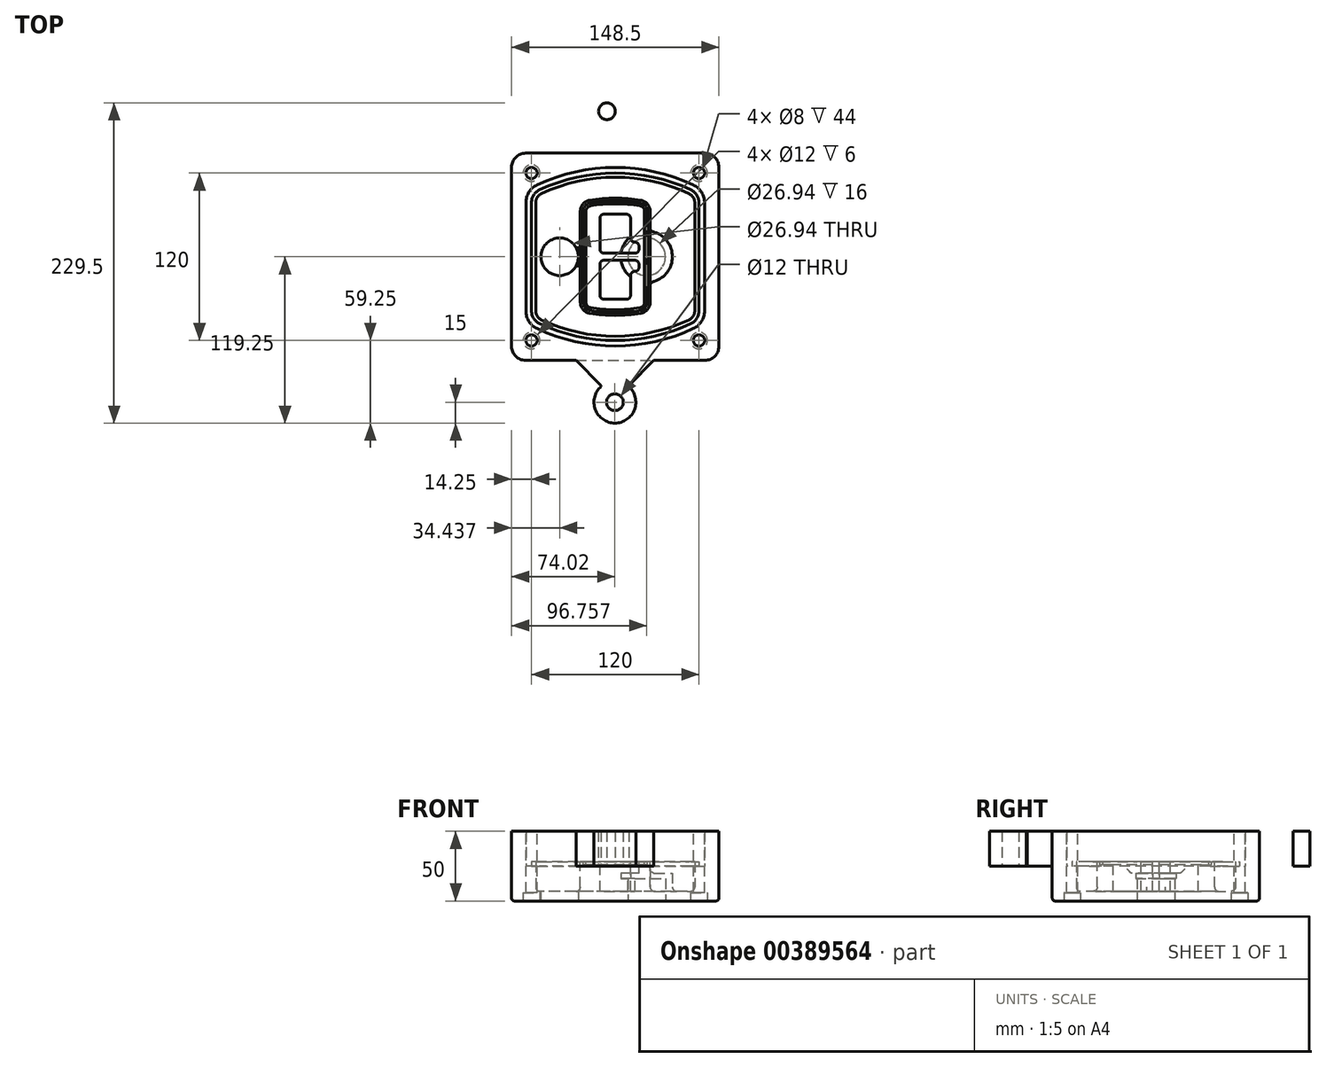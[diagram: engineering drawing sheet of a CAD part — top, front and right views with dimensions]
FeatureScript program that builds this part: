
annotation { "Feature Type Name" : "Feature", "Feature Type Description" : "" }
export const myFeature = defineFeature(function(context is Context, id is Id, definition is map)
    precondition{}
    {
        {
            var Q0;
            Q0=qCreatedBy(makeId("Top.planeOp"),FACE);
            var sketch = newSketch(context, id + "F0", { "sketchPlane" : qUnion([Q0])});
            skPoint(sketch, "E0.rect.middle", {"position": v(0, 0) * mm});
            skLineSegment(sketch, "E1.bottom", {"start": v(-64.25, -74.25) * mm, "end": v(64.25, -74.25) * mm});
            skLineSegment(sketch, "E1.top", {"start": v(-64.25, 74.25) * mm, "end": v(64.25, 74.25) * mm});
            skLineSegment(sketch, "E1.left", {"start": v(-74.25, -64.25) * mm, "end": v(-74.25, 64.25) * mm});
            skLineSegment(sketch, "E1.right", {"start": v(74.25, -64.25) * mm, "end": v(74.25, 64.25) * mm});
            skLineSegment(sketch, "E2", {"start": v(-74.25, 74.25) * mm, "end": v(74.25, -74.25) * mm, "construction": true});
            skLineSegment(sketch, "E3", {"start": v(74.25, 74.25) * mm, "end": v(-74.25, -74.25) * mm, "construction": true});
            skCircle(sketch, "E4", {"center": v(-60, 60) * mm, "radius": 4 * mm});
            skCircle(sketch, "E5", {"center": v(60, 60) * mm, "radius": 4 * mm});
            skCircle(sketch, "E6", {"center": v(60, -60) * mm, "radius": 4 * mm});
            skCircle(sketch, "E7", {"center": v(-60, -60) * mm, "radius": 4 * mm});
            skLineSegment(sketch, "E8", {"start": v(-60, 60) * mm, "end": v(60, 60) * mm, "construction": true});
            skLineSegment(sketch, "E9", {"start": v(60, 60) * mm, "end": v(60, -60) * mm, "construction": true});
            skLineSegment(sketch, "E10", {"start": v(60, -60) * mm, "end": v(-60, -60) * mm, "construction": true});
            skLineSegment(sketch, "E11", {"start": v(-60, -60) * mm, "end": v(-60, 60) * mm, "construction": true});
            skLineSegment(sketch, "E12", {"start": v(-60, 38.83) * mm, "end": v(-60, -38.83) * mm});
            skLineSegment(sketch, "E13", {"start": v(60, 38.83) * mm, "end": v(60, -38.83) * mm});
            skArc(sketch, "E14", {"start": v(54.26, 47.88) * mm, "mid": v(0, 60) * mm, "end": v(-54.26, 47.88) * mm});
            skArc(sketch, "E15", {"start": v(-54.26, -47.88) * mm, "mid": v(0, -60) * mm, "end": v(54.26, -47.88) * mm});
            skLineSegment(sketch, "E16", {"start": v(-60, 0) * mm, "end": v(60, 0) * mm, "construction": true});
            skPoint(sketch, "E17.visualSharp", {"position": v(-60, -45) * mm});
            skArc(sketch, "E17.filletArc", {"start": v(-60, -38.83) * mm, "mid": v(-58.44, -44.2) * mm, "end": v(-54.26, -47.88) * mm});
            skPoint(sketch, "E18.visualSharp", {"position": v(-60, 45) * mm});
            skArc(sketch, "E18.filletArc", {"start": v(-54.26, 47.88) * mm, "mid": v(-58.44, 44.2) * mm, "end": v(-60, 38.83) * mm});
            skPoint(sketch, "E19.visualSharp", {"position": v(60, 45) * mm});
            skArc(sketch, "E19.filletArc", {"start": v(60, 38.83) * mm, "mid": v(58.44, 44.2) * mm, "end": v(54.26, 47.88) * mm});
            skPoint(sketch, "E20.visualSharp", {"position": v(60, -45) * mm});
            skArc(sketch, "E20.filletArc", {"start": v(54.26, -47.88) * mm, "mid": v(58.44, -44.2) * mm, "end": v(60, -38.83) * mm});
            skPoint(sketch, "E21.visualSharp", {"position": v(-74.25, 74.25) * mm});
            skArc(sketch, "E21.filletArc", {"start": v(-64.25, 74.25) * mm, "mid": v(-71.32, 71.32) * mm, "end": v(-74.25, 64.25) * mm});
            skPoint(sketch, "E22.visualSharp", {"position": v(74.25, 74.25) * mm});
            skArc(sketch, "E22.filletArc", {"start": v(74.25, 64.25) * mm, "mid": v(71.32, 71.32) * mm, "end": v(64.25, 74.25) * mm});
            skPoint(sketch, "E23.visualSharp", {"position": v(74.25, -74.25) * mm});
            skArc(sketch, "E23.filletArc", {"start": v(64.25, -74.25) * mm, "mid": v(71.32, -71.32) * mm, "end": v(74.25, -64.25) * mm});
            skPoint(sketch, "E24.visualSharp", {"position": v(-74.25, -74.25) * mm});
            skArc(sketch, "E24.filletArc", {"start": v(-74.25, -64.25) * mm, "mid": v(-71.32, -71.32) * mm, "end": v(-64.25, -74.25) * mm});
            skArc(sketch, "E25.0", {"start": v(57, 38.83) * mm, "mid": v(55.9, 42.58) * mm, "end": v(52.98, 45.17) * mm});
            skLineSegment(sketch, "E25.1", {"start": v(57, 38.83) * mm, "end": v(57, -38.83) * mm});
            skArc(sketch, "E25.2", {"start": v(52.98, -45.17) * mm, "mid": v(55.9, -42.58) * mm, "end": v(57, -38.83) * mm});
            skArc(sketch, "E25.3", {"start": v(-52.98, -45.17) * mm, "mid": v(0, -57) * mm, "end": v(52.98, -45.17) * mm});
            skArc(sketch, "E25.4", {"start": v(-57, -38.83) * mm, "mid": v(-55.9, -42.58) * mm, "end": v(-52.98, -45.17) * mm});
            skArc(sketch, "E25.5", {"start": v(52.98, 45.17) * mm, "mid": v(0, 57) * mm, "end": v(-52.98, 45.17) * mm});
            skLineSegment(sketch, "E25.6", {"start": v(-57, 38.83) * mm, "end": v(-57, -38.83) * mm});
            skArc(sketch, "E25.7", {"start": v(-52.98, 45.17) * mm, "mid": v(-55.9, 42.58) * mm, "end": v(-57, 38.83) * mm});
            skArc(sketch, "E26.0", {"start": v(-55.96, 51.5) * mm, "mid": v(-61.82, 46.33) * mm, "end": v(-64, 38.83) * mm});
            skArc(sketch, "E26.1", {"start": v(55.96, 51.5) * mm, "mid": v(0, 64) * mm, "end": v(-55.96, 51.5) * mm});
            skArc(sketch, "E26.2", {"start": v(64, 38.83) * mm, "mid": v(61.82, 46.33) * mm, "end": v(55.96, 51.5) * mm});
            skLineSegment(sketch, "E26.3", {"start": v(64, 38.83) * mm, "end": v(64, -38.83) * mm});
            skArc(sketch, "E26.4", {"start": v(55.96, -51.5) * mm, "mid": v(61.82, -46.33) * mm, "end": v(64, -38.83) * mm});
            skLineSegment(sketch, "E26.5", {"start": v(-64, 38.83) * mm, "end": v(-64, -38.83) * mm});
            skArc(sketch, "E26.6", {"start": v(-55.96, -51.5) * mm, "mid": v(0, -64) * mm, "end": v(55.96, -51.5) * mm});
            skArc(sketch, "E26.7", {"start": v(-64, -38.83) * mm, "mid": v(-61.82, -46.33) * mm, "end": v(-55.96, -51.5) * mm});
            skLineSegment(sketch, "E27", {"start": v(9.02, 104.25) * mm, "end": v(9.02, 90.33) * mm, "construction": true});
            skLineSegment(sketch, "E28", {"start": v(9.02, 90.33) * mm, "end": v(25.1, 74.25) * mm});
            skLineSegment(sketch, "E29", {"start": v(-20.98, 104.25) * mm, "end": v(-20.98, 92.25) * mm});
            skLineSegment(sketch, "E30", {"start": v(-20.98, 92.25) * mm, "end": v(-38.98, 74.25) * mm});
            skArc(sketch, "E31", {"start": v(9.02, 104.25) * mm, "mid": v(-5.98, 119.25) * mm, "end": v(-20.98, 104.25) * mm});
            skCircle(sketch, "E32", {"center": v(-5.98, 104.25) * mm, "radius": 6 * mm});
            skPoint(sketch, "E33.positionSnap0", {"position": v(0, -74.25) * mm});
            skLineSegment(sketch, "E34", {"start": v(9.64, -92.95) * mm, "end": v(9.64, -92.25) * mm});
            skLineSegment(sketch, "E35", {"start": v(9.64, -92.25) * mm, "end": v(27.64, -74.25) * mm});
            skLineSegment(sketch, "E36", {"start": v(-10.1, -92.95) * mm, "end": v(-10.1, -92.25) * mm});
            skLineSegment(sketch, "E37", {"start": v(-10.1, -92.25) * mm, "end": v(-28.1, -74.25) * mm});
            skArc(sketch, "E38", {"start": v(-10.1, -92.95) * mm, "mid": v(-0.23, -119.25) * mm, "end": v(9.64, -92.95) * mm});
            skCircle(sketch, "E39", {"center": v(-0.23, -104.25) * mm, "radius": 6 * mm});
            skSolve(sketch);
        }
        {
            var Q0;
            Q0=makeQuery(id+"F0.imprint","IMPRINT",FACE,{"disambiguationData":[TD([[makeQuery(id+"F0.imprint","IMPRINT",EDGE,{"derivedFrom":sQuery(id+"F0.wireOp",EDGE,"E1.bottom")}),1.0]])]});
            var Q1;
            Q1=makeQuery(id+"F0.imprint","IMPRINT",FACE,{"disambiguationData":[TD([[makeQuery(id+"F0.imprint","IMPRINT",EDGE,{"derivedFrom":sQuery(id+"F0.wireOp",EDGE,"E12")}),1.0]])]});
            var Q2;
            Q2=makeQuery(id+"F0.imprint","IMPRINT",FACE,{"disambiguationData":[TD([[makeQuery(id+"F0.imprint","IMPRINT",EDGE,{"derivedFrom":sQuery(id+"F0.wireOp",EDGE,"E25.0")}),1.0]])]});
            var Q3;
            Q3=makeQuery(id+"F0.imprint","IMPRINT",FACE,{"disambiguationData":[TD([[makeQuery(id+"F0.imprint","IMPRINT",EDGE,{"derivedFrom":sQuery(id+"F0.wireOp",EDGE,"E12")}),-1.0]])]});
            extrude(context, id + "F1", {"entities" : qUnion([Q0, Q1, Q2, Q3]), "oppositeDirection" : true, "depth" : 25 * mm});
        }
        {
            var Q0;
            Q0=makeQuery(id+"F0.imprint","IMPRINT",FACE,{"disambiguationData":[TD([[makeQuery(id+"F0.imprint","IMPRINT",EDGE,{"derivedFrom":sQuery(id+"F0.wireOp",EDGE,"E12")}),1.0]])]});
            extrude(context, id + "F2", {"entities" : qUnion([Q0]), "operationType" : NewBodyOperationType.ADD, "depth" : 3 * mm});
        }
        {
            var Q0;
            Q0=makeQuery(id+"F0.imprint","IMPRINT",FACE,{"disambiguationData":[TD([[makeQuery(id+"F0.imprint","IMPRINT",EDGE,{"derivedFrom":sQuery(id+"F0.wireOp",EDGE,"E25.0")}),1.0]])]});
            extrude(context, id + "F3", {"entities" : qUnion([Q0]), "operationType" : NewBodyOperationType.REMOVE, "oppositeDirection" : true, "depth" : 18 * mm});
        }
        {
            var Q0;
            Q0=makeQuery(id+"F2.opExtrude","CAP_FACE",FACE,{"disambiguationData":[OSD([sQuery(id+"F0.wireOp",EDGE,"E12"),sQuery(id+"F0.wireOp",EDGE,"E13"),sQuery(id+"F0.wireOp",EDGE,"E14"),sQuery(id+"F0.wireOp",EDGE,"E15"),sQuery(id+"F0.wireOp",EDGE,"E17.filletArc"),sQuery(id+"F0.wireOp",EDGE,"E18.filletArc"),sQuery(id+"F0.wireOp",EDGE,"E19.filletArc"),sQuery(id+"F0.wireOp",EDGE,"E20.filletArc"),sQuery(id+"F0.wireOp",EDGE,"E25.0"),sQuery(id+"F0.wireOp",EDGE,"E25.1"),sQuery(id+"F0.wireOp",EDGE,"E25.2"),sQuery(id+"F0.wireOp",EDGE,"E25.3"),sQuery(id+"F0.wireOp",EDGE,"E25.4"),sQuery(id+"F0.wireOp",EDGE,"E25.5"),sQuery(id+"F0.wireOp",EDGE,"E25.6"),sQuery(id+"F0.wireOp",EDGE,"E25.7")])],"isStart":false});
            var sketch = newSketch(context, id + "F4", { "sketchPlane" : qUnion([Q0])});
            skArc(sketch, "E40.0", {"start": v(-18.34, -40.45) * mm, "mid": v(0, -42) * mm, "end": v(18.34, -40.45) * mm});
            skArc(sketch, "E41.0", {"start": v(18.34, 40.45) * mm, "mid": v(0, 42) * mm, "end": v(-18.34, 40.45) * mm});
            skLineSegment(sketch, "E42", {"start": v(-25, 32.57) * mm, "end": v(-25, -32.57) * mm});
            skLineSegment(sketch, "E43", {"start": v(25, 32.57) * mm, "end": v(25, -32.57) * mm});
            skLineSegment(sketch, "E44", {"start": v(-25, 39.1) * mm, "end": v(25, 39.1) * mm, "construction": true});
            skLineSegment(sketch, "E45", {"start": v(-25, -39.1) * mm, "end": v(25, -39.1) * mm, "construction": true});
            skPoint(sketch, "E46.visualSharp", {"position": v(-25, 39.1) * mm});
            skArc(sketch, "E46.filletArc", {"start": v(-18.34, 40.45) * mm, "mid": v(-23.11, 37.73) * mm, "end": v(-25, 32.57) * mm});
            skPoint(sketch, "E47.visualSharp", {"position": v(25, 39.1) * mm});
            skArc(sketch, "E47.filletArc", {"start": v(25, 32.57) * mm, "mid": v(23.11, 37.73) * mm, "end": v(18.34, 40.45) * mm});
            skPoint(sketch, "E48.visualSharp", {"position": v(25, -39.1) * mm});
            skArc(sketch, "E48.filletArc", {"start": v(18.34, -40.45) * mm, "mid": v(23.11, -37.73) * mm, "end": v(25, -32.57) * mm});
            skPoint(sketch, "E49.visualSharp", {"position": v(-25, -39.1) * mm});
            skArc(sketch, "E49.filletArc", {"start": v(-25, -32.57) * mm, "mid": v(-23.11, -37.73) * mm, "end": v(-18.34, -40.45) * mm});
            skArc(sketch, "E50.0", {"start": v(52.98, 45.17) * mm, "mid": v(0, 57) * mm, "end": v(-52.98, 45.17) * mm});
            skArc(sketch, "E50.1", {"start": v(-52.98, 45.17) * mm, "mid": v(-55.9, 42.58) * mm, "end": v(-57, 38.83) * mm});
            skLineSegment(sketch, "E50.2", {"start": v(-57, 38.83) * mm, "end": v(-57, -38.83) * mm});
            skArc(sketch, "E50.3", {"start": v(-57, -38.83) * mm, "mid": v(-55.9, -42.58) * mm, "end": v(-52.98, -45.17) * mm});
            skArc(sketch, "E50.4", {"start": v(-52.98, -45.17) * mm, "mid": v(0, -57) * mm, "end": v(52.98, -45.17) * mm});
            skArc(sketch, "E50.5", {"start": v(52.98, -45.17) * mm, "mid": v(55.9, -42.58) * mm, "end": v(57, -38.83) * mm});
            skLineSegment(sketch, "E50.6", {"start": v(57, 38.83) * mm, "end": v(57, -38.83) * mm});
            skArc(sketch, "E50.7", {"start": v(57, 38.83) * mm, "mid": v(55.9, 42.58) * mm, "end": v(52.98, 45.17) * mm});
            skLineSegment(sketch, "E51.0", {"start": v(23, 32.57) * mm, "end": v(23, -32.57) * mm});
            skArc(sketch, "E51.1", {"start": v(18, -38.48) * mm, "mid": v(21.58, -36.44) * mm, "end": v(23, -32.57) * mm});
            skArc(sketch, "E51.2", {"start": v(-18, -38.48) * mm, "mid": v(0, -40) * mm, "end": v(18, -38.48) * mm});
            skArc(sketch, "E51.3", {"start": v(-23, -32.57) * mm, "mid": v(-21.58, -36.44) * mm, "end": v(-18, -38.48) * mm});
            skLineSegment(sketch, "E51.4", {"start": v(-23, 32.57) * mm, "end": v(-23, -32.57) * mm});
            skArc(sketch, "E51.5", {"start": v(23, 32.57) * mm, "mid": v(21.58, 36.44) * mm, "end": v(18, 38.48) * mm});
            skArc(sketch, "E51.6", {"start": v(-18, 38.48) * mm, "mid": v(-21.58, 36.44) * mm, "end": v(-23, 32.57) * mm});
            skArc(sketch, "E51.7", {"start": v(18, 38.48) * mm, "mid": v(0, 40) * mm, "end": v(-18, 38.48) * mm});
            skArc(sketch, "E52.0", {"start": v(21, 32.57) * mm, "mid": v(20.06, 35.15) * mm, "end": v(17.67, 36.5) * mm});
            skLineSegment(sketch, "E52.1", {"start": v(21, 32.57) * mm, "end": v(21, -32.57) * mm});
            skArc(sketch, "E52.2", {"start": v(17.67, -36.5) * mm, "mid": v(20.06, -35.15) * mm, "end": v(21, -32.57) * mm});
            skArc(sketch, "E52.3", {"start": v(-17.67, -36.5) * mm, "mid": v(0, -38) * mm, "end": v(17.67, -36.5) * mm});
            skArc(sketch, "E52.4", {"start": v(-21, -32.57) * mm, "mid": v(-20.06, -35.15) * mm, "end": v(-17.67, -36.5) * mm});
            skArc(sketch, "E52.5", {"start": v(17.67, 36.5) * mm, "mid": v(0, 38) * mm, "end": v(-17.67, 36.5) * mm});
            skLineSegment(sketch, "E52.6", {"start": v(-21, 32.57) * mm, "end": v(-21, -32.57) * mm});
            skArc(sketch, "E52.7", {"start": v(-17.67, 36.5) * mm, "mid": v(-20.06, 35.15) * mm, "end": v(-21, 32.57) * mm});
            skLineSegment(sketch, "E53", {"start": v(-25, 0) * mm, "end": v(25, 0) * mm, "construction": true});
            skLineSegment(sketch, "E54", {"start": v(-11, 5.5) * mm, "end": v(-11, 27.5) * mm});
            skLineSegment(sketch, "E55", {"start": v(-8, 30.5) * mm, "end": v(8, 30.5) * mm});
            skLineSegment(sketch, "E56", {"start": v(11, 27.5) * mm, "end": v(11, 13.5) * mm});
            skLineSegment(sketch, "E57", {"start": v(14, 10.5) * mm, "end": v(14, 10.5) * mm});
            skLineSegment(sketch, "E58", {"start": v(17, 7.5) * mm, "end": v(17, 5.5) * mm});
            skLineSegment(sketch, "E59", {"start": v(14, 2.5) * mm, "end": v(-8, 2.5) * mm});
            skPoint(sketch, "E60.visualSharp", {"position": v(-11, 30.5) * mm});
            skArc(sketch, "E60.filletArc", {"start": v(-8, 30.5) * mm, "mid": v(-10.12, 29.62) * mm, "end": v(-11, 27.5) * mm});
            skPoint(sketch, "E61.visualSharp", {"position": v(11, 30.5) * mm});
            skArc(sketch, "E61.filletArc", {"start": v(11, 27.5) * mm, "mid": v(10.12, 29.62) * mm, "end": v(8, 30.5) * mm});
            skPoint(sketch, "E62.visualSharp", {"position": v(11, 10.5) * mm});
            skArc(sketch, "E62.filletArc", {"start": v(11, 13.5) * mm, "mid": v(11.88, 11.38) * mm, "end": v(14, 10.5) * mm});
            skPoint(sketch, "E63.visualSharp", {"position": v(17, 10.5) * mm});
            skArc(sketch, "E63.filletArc", {"start": v(17, 7.5) * mm, "mid": v(16.12, 9.62) * mm, "end": v(14, 10.5) * mm});
            skPoint(sketch, "E64.visualSharp", {"position": v(17, 2.5) * mm});
            skArc(sketch, "E64.filletArc", {"start": v(14, 2.5) * mm, "mid": v(16.12, 3.38) * mm, "end": v(17, 5.5) * mm});
            skPoint(sketch, "E65.visualSharp", {"position": v(-11, 2.5) * mm});
            skArc(sketch, "E65.filletArc", {"start": v(-11, 5.5) * mm, "mid": v(-10.12, 3.38) * mm, "end": v(-8, 2.5) * mm});
            skLineSegment(sketch, "E66.0.MirrorCS", {"start": v(14, -2.5) * mm, "end": v(-8, -2.5) * mm});
            skArc(sketch, "E67.0.MirrorCS", {"start": v(-11, -5.5) * mm, "mid": v(-10.12, -3.38) * mm, "end": v(-8, -2.5) * mm});
            skLineSegment(sketch, "E68.0.MirrorCS", {"start": v(-11, -5.5) * mm, "end": v(-11, -27.5) * mm});
            skArc(sketch, "E69.0.MirrorCS", {"start": v(-8, -30.5) * mm, "mid": v(-10.12, -29.62) * mm, "end": v(-11, -27.5) * mm});
            skLineSegment(sketch, "E70.0.MirrorCS", {"start": v(-8, -30.5) * mm, "end": v(8, -30.5) * mm});
            skArc(sketch, "E71.0.MirrorCS", {"start": v(11, -27.5) * mm, "mid": v(10.12, -29.62) * mm, "end": v(8, -30.5) * mm});
            skLineSegment(sketch, "E72.0.MirrorCS", {"start": v(11, -27.5) * mm, "end": v(11, -13.5) * mm});
            skArc(sketch, "E73.0.MirrorCS", {"start": v(11, -13.5) * mm, "mid": v(11.88, -11.38) * mm, "end": v(14, -10.5) * mm});
            skArc(sketch, "E74.0.MirrorCS", {"start": v(17, -7.5) * mm, "mid": v(16.12, -9.62) * mm, "end": v(14, -10.5) * mm});
            skLineSegment(sketch, "E75.0.MirrorCS", {"start": v(17, -7.5) * mm, "end": v(17, -5.5) * mm});
            skArc(sketch, "E76.0.MirrorCS", {"start": v(14, -2.5) * mm, "mid": v(16.12, -3.38) * mm, "end": v(17, -5.5) * mm});
            skSolve(sketch);
        }
        {
            var Q0;
            Q0=makeQuery(id+"F4.imprint","IMPRINT",FACE,{"disambiguationData":[TD([[makeQuery(id+"F4.imprint","IMPRINT",EDGE,{"derivedFrom":sQuery(id+"F4.wireOp",EDGE,"E40.0")}),1.0]])]});
            var Q1;
            Q1=makeQuery(id+"F4.imprint","IMPRINT",FACE,{"disambiguationData":[TD([[makeQuery(id+"F4.imprint","IMPRINT",EDGE,{"derivedFrom":sQuery(id+"F4.wireOp",EDGE,"E51.0")}),-1.0]])]});
            var Q2;
            Q2=makeQuery(id+"F4.imprint","IMPRINT",FACE,{"disambiguationData":[TD([[makeQuery(id+"F4.imprint","IMPRINT",EDGE,{"derivedFrom":sQuery(id+"F4.wireOp",EDGE,"E52.0")}),1.0]])]});
            extrude(context, id + "F5", {"entities" : qUnion([Q0, Q1, Q2]), "operationType" : NewBodyOperationType.ADD, "endBound" : BoundingType.UP_TO_NEXT, "oppositeDirection" : true, "depth" : 25 * mm});
        }
        {
            var Q0;
            Q0=makeQuery(id+"F4.imprint","IMPRINT",FACE,{"disambiguationData":[TD([[makeQuery(id+"F4.imprint","IMPRINT",EDGE,{"derivedFrom":sQuery(id+"F4.wireOp",EDGE,"E51.0")}),-1.0]])]});
            extrude(context, id + "F6", {"entities" : qUnion([Q0]), "operationType" : NewBodyOperationType.REMOVE, "oppositeDirection" : true, "depth" : 2 * mm});
        }
        {
            var Q0;
            Q0=makeQuery(id+"F1.opExtrude","CAP_FACE",FACE,{"disambiguationData":[OSD([sQuery(id+"F0.wireOp",EDGE,"E1.bottom"),sQuery(id+"F0.wireOp",EDGE,"E1.top"),sQuery(id+"F0.wireOp",EDGE,"E1.left"),sQuery(id+"F0.wireOp",EDGE,"E1.right"),sQuery(id+"F0.wireOp",EDGE,"E4"),sQuery(id+"F0.wireOp",EDGE,"E5"),sQuery(id+"F0.wireOp",EDGE,"E6"),sQuery(id+"F0.wireOp",EDGE,"E7"),sQuery(id+"F0.wireOp",EDGE,"E21.filletArc"),sQuery(id+"F0.wireOp",EDGE,"E22.filletArc"),sQuery(id+"F0.wireOp",EDGE,"E23.filletArc"),sQuery(id+"F0.wireOp",EDGE,"E24.filletArc")])],"isStart":false});
            var sketch = newSketch(context, id + "F7", { "sketchPlane" : qUnion([Q0])});
            skCircle(sketch, "E77", {"center": v(22.5, 0) * mm, "radius": 13.47 * mm});
            skCircle(sketch, "E78", {"center": v(-39.81, 0) * mm, "radius": 13.47 * mm});
            skLineSegment(sketch, "E79", {"start": v(74.25, 0) * mm, "end": v(-74.25, 0) * mm});
            skCircle(sketch, "E80", {"center": v(22.5, 0) * mm, "radius": 18.47 * mm});
            skCircle(sketch, "E81", {"center": v(60, -60) * mm, "radius": 6 * mm});
            skCircle(sketch, "E82", {"center": v(-60, -60) * mm, "radius": 6 * mm});
            skCircle(sketch, "E83", {"center": v(-60, 60) * mm, "radius": 6 * mm});
            skCircle(sketch, "E84", {"center": v(60, 60) * mm, "radius": 6 * mm});
            skSolve(sketch);
        }
        {
            var Q0;
            {var subQ1=sQuery(id+"F7.wireOp",EDGE,"E79");var subQ4=sQuery(id+"F7.wireOp",EDGE,"E77");var subQ6=makeQuery(id+"F7.imprint","INTERSECT",VERTEX,{"disambiguationData":[OD(0.0)],"derivedFrom":[subQ4,subQ1]});Q0=makeQuery(id+"F7.imprint","IMPRINT",FACE,{"disambiguationData":[TD([[makeQuery(id+"F7.imprint","IMPRINT",EDGE,{"disambiguationData":[TD([[subQ6,-1.0]])],"derivedFrom":subQ4}),-1.0]])]});}
            var Q1;
            {var subQ0=sQuery(id+"F7.wireOp",EDGE,"E79");var subQ1=sQuery(id+"F7.wireOp",EDGE,"E77");var subQ3=makeQuery(id+"F7.imprint","INTERSECT",VERTEX,{"disambiguationData":[OD(0.0)],"derivedFrom":[subQ1,subQ0]});Q1=makeQuery(id+"F7.imprint","IMPRINT",FACE,{"disambiguationData":[TD([[makeQuery(id+"F7.imprint","IMPRINT",EDGE,{"disambiguationData":[TD([[subQ3,-1.0]])],"derivedFrom":subQ1}),1.0]])]});}
            var Q2;
            {var subQ0=sQuery(id+"F7.wireOp",EDGE,"E79");var subQ1=sQuery(id+"F7.wireOp",EDGE,"E77");var subQ3=makeQuery(id+"F7.imprint","INTERSECT",VERTEX,{"disambiguationData":[OD(0.0)],"derivedFrom":[subQ1,subQ0]});Q2=makeQuery(id+"F7.imprint","IMPRINT",FACE,{"disambiguationData":[TD([[makeQuery(id+"F7.imprint","IMPRINT",EDGE,{"disambiguationData":[TD([[subQ3,1.0]])],"derivedFrom":subQ1}),1.0]])]});}
            var Q3;
            {var subQ1=sQuery(id+"F7.wireOp",EDGE,"E79");var subQ4=sQuery(id+"F7.wireOp",EDGE,"E77");var subQ6=makeQuery(id+"F7.imprint","INTERSECT",VERTEX,{"disambiguationData":[OD(0.0)],"derivedFrom":[subQ4,subQ1]});Q3=makeQuery(id+"F7.imprint","IMPRINT",FACE,{"disambiguationData":[TD([[makeQuery(id+"F7.imprint","IMPRINT",EDGE,{"disambiguationData":[TD([[subQ6,1.0]])],"derivedFrom":subQ4}),-1.0]])]});}
            extrude(context, id + "F8", {"entities" : qUnion([Q0, Q1, Q2, Q3]), "operationType" : NewBodyOperationType.ADD, "oppositeDirection" : true, "depth" : 20 * mm});
        }
        {
            var Q0;
            {var subQ0=sQuery(id+"F7.wireOp",EDGE,"E79");var subQ1=sQuery(id+"F7.wireOp",EDGE,"E77");var subQ3=makeQuery(id+"F7.imprint","INTERSECT",VERTEX,{"disambiguationData":[OD(0.0)],"derivedFrom":[subQ1,subQ0]});Q0=makeQuery(id+"F7.imprint","IMPRINT",FACE,{"disambiguationData":[TD([[makeQuery(id+"F7.imprint","IMPRINT",EDGE,{"disambiguationData":[TD([[subQ3,-1.0]])],"derivedFrom":subQ1}),1.0]])]});}
            var Q1;
            {var subQ0=sQuery(id+"F7.wireOp",EDGE,"E79");var subQ1=sQuery(id+"F7.wireOp",EDGE,"E77");var subQ3=makeQuery(id+"F7.imprint","INTERSECT",VERTEX,{"disambiguationData":[OD(0.0)],"derivedFrom":[subQ1,subQ0]});Q1=makeQuery(id+"F7.imprint","IMPRINT",FACE,{"disambiguationData":[TD([[makeQuery(id+"F7.imprint","IMPRINT",EDGE,{"disambiguationData":[TD([[subQ3,1.0]])],"derivedFrom":subQ1}),1.0]])]});}
            extrude(context, id + "F9", {"entities" : qUnion([Q0, Q1]), "operationType" : NewBodyOperationType.REMOVE, "oppositeDirection" : true, "depth" : 16 * mm});
        }
        {
            var Q0;
            {var subQ0=sQuery(id+"F7.wireOp",EDGE,"E79");var subQ1=sQuery(id+"F7.wireOp",EDGE,"E78");var subQ3=makeQuery(id+"F7.imprint","INTERSECT",VERTEX,{"disambiguationData":[OD(0.0)],"derivedFrom":[subQ1,subQ0]});Q0=makeQuery(id+"F7.imprint","IMPRINT",FACE,{"disambiguationData":[TD([[makeQuery(id+"F7.imprint","IMPRINT",EDGE,{"disambiguationData":[TD([[subQ3,-1.0]])],"derivedFrom":subQ1}),1.0]])]});}
            var Q1;
            {var subQ0=sQuery(id+"F7.wireOp",EDGE,"E79");var subQ1=sQuery(id+"F7.wireOp",EDGE,"E78");var subQ3=makeQuery(id+"F7.imprint","INTERSECT",VERTEX,{"disambiguationData":[OD(0.0)],"derivedFrom":[subQ1,subQ0]});Q1=makeQuery(id+"F7.imprint","IMPRINT",FACE,{"disambiguationData":[TD([[makeQuery(id+"F7.imprint","IMPRINT",EDGE,{"disambiguationData":[TD([[subQ3,1.0]])],"derivedFrom":subQ1}),1.0]])]});}
            extrude(context, id + "F10", {"entities" : qUnion([Q0, Q1]), "operationType" : NewBodyOperationType.REMOVE, "oppositeDirection" : true, "depth" : 25 * mm});
        }
        {
            var Q0;
            Q0=makeQuery(id+"F7.imprint","IMPRINT",FACE,{"disambiguationData":[TD([[makeQuery(id+"F7.imprint","IMPRINT",EDGE,{"derivedFrom":sQuery(id+"F7.wireOp",EDGE,"E81")}),1.0]])]});
            var Q1;
            Q1=makeQuery(id+"F7.imprint","IMPRINT",FACE,{"disambiguationData":[TD([[makeQuery(id+"F7.imprint","IMPRINT",EDGE,{"derivedFrom":makeQuery(id+"F1.opExtrude","CAP_EDGE",EDGE,{"disambiguationData":[OSD([sQuery(id+"F0.wireOp",EDGE,"E5")])],"isStart":false})}),-1.0]])]});
            var Q2;
            Q2=makeQuery(id+"F7.imprint","IMPRINT",FACE,{"disambiguationData":[TD([[makeQuery(id+"F7.imprint","IMPRINT",EDGE,{"derivedFrom":sQuery(id+"F7.wireOp",EDGE,"E82")}),1.0]])]});
            var Q3;
            Q3=makeQuery(id+"F7.imprint","IMPRINT",FACE,{"disambiguationData":[TD([[makeQuery(id+"F7.imprint","IMPRINT",EDGE,{"derivedFrom":makeQuery(id+"F1.opExtrude","CAP_EDGE",EDGE,{"disambiguationData":[OSD([sQuery(id+"F0.wireOp",EDGE,"E4")])],"isStart":false})}),-1.0]])]});
            var Q4;
            Q4=makeQuery(id+"F7.imprint","IMPRINT",FACE,{"disambiguationData":[TD([[makeQuery(id+"F7.imprint","IMPRINT",EDGE,{"derivedFrom":sQuery(id+"F7.wireOp",EDGE,"E83")}),1.0]])]});
            var Q5;
            Q5=makeQuery(id+"F7.imprint","IMPRINT",FACE,{"disambiguationData":[TD([[makeQuery(id+"F7.imprint","IMPRINT",EDGE,{"derivedFrom":makeQuery(id+"F1.opExtrude","CAP_EDGE",EDGE,{"disambiguationData":[OSD([sQuery(id+"F0.wireOp",EDGE,"E7")])],"isStart":false})}),-1.0]])]});
            var Q6;
            Q6=makeQuery(id+"F7.imprint","IMPRINT",FACE,{"disambiguationData":[TD([[makeQuery(id+"F7.imprint","IMPRINT",EDGE,{"derivedFrom":sQuery(id+"F7.wireOp",EDGE,"E84")}),1.0]])]});
            var Q7;
            Q7=makeQuery(id+"F7.imprint","IMPRINT",FACE,{"disambiguationData":[TD([[makeQuery(id+"F7.imprint","IMPRINT",EDGE,{"derivedFrom":makeQuery(id+"F1.opExtrude","CAP_EDGE",EDGE,{"disambiguationData":[OSD([sQuery(id+"F0.wireOp",EDGE,"E6")])],"isStart":false})}),-1.0]])]});
            extrude(context, id + "F11", {"entities" : qUnion([Q0, Q1, Q2, Q3, Q4, Q5, Q6, Q7]), "operationType" : NewBodyOperationType.REMOVE, "oppositeDirection" : true, "depth" : 6 * mm});
        }
        {
            var Q0;
            Q0=makeQuery(id+"F9.boolean.opBoolean","COPY",FACE,{"derivedFrom":makeQuery(id+"F9.opExtrude","CAP_FACE",FACE,{"disambiguationData":[OSD([sQuery(id+"F7.wireOp",EDGE,"E77")])],"isStart":false})});
            var sketch = newSketch(context, id + "F12", { "sketchPlane" : qUnion([Q0])});
            skArc(sketch, "E85.0", {"start": v(11, 14.45) * mm, "mid": v(6.45, 9.13) * mm, "end": v(4.2, 2.5) * mm});
            skArc(sketch, "E85.1", {"start": v(4.2, -2.5) * mm, "mid": v(6.45, -9.13) * mm, "end": v(11, -14.45) * mm});
            skLineSegment(sketch, "E86", {"start": v(4.2, -2.5) * mm, "end": v(14, -2.5) * mm});
            skLineSegment(sketch, "E87.0", {"start": v(14, 2.5) * mm, "end": v(4.2, 2.5) * mm});
            skArc(sketch, "E87.1", {"start": v(14, 2.5) * mm, "mid": v(16.12, 3.38) * mm, "end": v(17, 5.5) * mm});
            skLineSegment(sketch, "E87.2", {"start": v(17, 7.5) * mm, "end": v(17, 5.5) * mm});
            skArc(sketch, "E87.3", {"start": v(17, 7.5) * mm, "mid": v(16.12, 9.62) * mm, "end": v(14, 10.5) * mm});
            skArc(sketch, "E87.4", {"start": v(11, 13.5) * mm, "mid": v(11.88, 11.38) * mm, "end": v(14, 10.5) * mm});
            skLineSegment(sketch, "E87.5", {"start": v(11, 14.45) * mm, "end": v(11, 13.5) * mm});
            skLineSegment(sketch, "E87.7", {"start": v(14, -2.5) * mm, "end": v(4.2, -2.5) * mm});
            skArc(sketch, "E87.8", {"start": v(14, -2.5) * mm, "mid": v(16.12, -3.38) * mm, "end": v(17, -5.5) * mm});
            skLineSegment(sketch, "E87.9", {"start": v(17, -7.5) * mm, "end": v(17, -5.5) * mm});
            skArc(sketch, "E87.10", {"start": v(17, -7.5) * mm, "mid": v(16.12, -9.62) * mm, "end": v(14, -10.5) * mm});
            skArc(sketch, "E87.11", {"start": v(11, -13.5) * mm, "mid": v(11.88, -11.38) * mm, "end": v(14, -10.5) * mm});
            skLineSegment(sketch, "E87.12", {"start": v(11, -14.45) * mm, "end": v(11, -13.5) * mm});
            skPoint(sketch, "E88.orphan", {"position": v(11, -27.5) * mm});
            skPoint(sketch, "E89.orphan", {"position": v(-8, -2.5) * mm});
            skPoint(sketch, "E90.orphan", {"position": v(-8, 2.5) * mm});
            skPoint(sketch, "E91.orphan", {"position": v(11, 27.5) * mm});
            skSolve(sketch);
        }
        {
            var Q0;
            {var subQ7=sQuery(id+"F12.wireOp",EDGE,"E85.0");var subQ14=sQuery(id+"F12.wireOp",EDGE,"E85.1");var subQ16=sQuery(id+"F12.wireOp",EDGE,"E87.1");var subQ18=sQuery(id+"F12.wireOp",EDGE,"E87.8");Q0=qUnion([makeQuery(id+"F12.imprint","IMPRINT",FACE,{"disambiguationData":[TD([[makeQuery(id+"F12.imprint","IMPRINT",EDGE,{"derivedFrom":subQ7}),1.0]])]}),makeQuery(id+"F12.imprint","IMPRINT",FACE,{"disambiguationData":[TD([[makeQuery(id+"F12.imprint","IMPRINT",EDGE,{"derivedFrom":subQ14}),1.0]])]}),makeQuery(id+"F12.imprint","IMPRINT",FACE,{"disambiguationData":[TD([[makeQuery(id+"F12.imprint","IMPRINT",EDGE,{"derivedFrom":subQ16}),1.0]])]}),makeQuery(id+"F12.imprint","IMPRINT",FACE,{"disambiguationData":[TD([[makeQuery(id+"F12.imprint","IMPRINT",EDGE,{"derivedFrom":subQ18}),-1.0]])]})]);}
            var Q1;
            Q1=makeQuery(id+"F5.boolean.opBoolean","SPLIT",FACE,{"disambiguationData":[TD([makeQuery(id+"F5.opExtrude","SWEPT_FACE",FACE,{"disambiguationData":[OSD([sQuery(id+"F4.wireOp",EDGE,"E54")])]})])],"derivedFrom":makeQuery(id+"F3.boolean.opBoolean","COPY",FACE,{"derivedFrom":makeQuery(id+"F3.opExtrude","CAP_FACE",FACE,{"disambiguationData":[OSD([sQuery(id+"F0.wireOp",EDGE,"E25.0"),sQuery(id+"F0.wireOp",EDGE,"E25.1"),sQuery(id+"F0.wireOp",EDGE,"E25.2"),sQuery(id+"F0.wireOp",EDGE,"E25.3"),sQuery(id+"F0.wireOp",EDGE,"E25.4"),sQuery(id+"F0.wireOp",EDGE,"E25.5"),sQuery(id+"F0.wireOp",EDGE,"E25.6"),sQuery(id+"F0.wireOp",EDGE,"E25.7")])],"isStart":false})})});
            extrude(context, id + "F13", {"entities" : qUnion([Q0]), "operationType" : NewBodyOperationType.REMOVE, "endBound" : BoundingType.UP_TO_SURFACE, "endBoundEntityFace" : qUnion([Q1]), "depth" : 25 * mm});
        }
        {
            var Q0;
            Q0=makeQuery(id+"F3.boolean.opBoolean","COPY",EDGE,{"derivedFrom":makeQuery(id+"F3.opExtrude","CAP_EDGE",EDGE,{"disambiguationData":[OSD([sQuery(id+"F0.wireOp",EDGE,"E25.6")])],"isStart":false})});
            var Q1;
            Q1=makeQuery(id+"F8.boolean.opBoolean","INTERSECT",EDGE,{"derivedFrom":[makeQuery(id+"F5.opExtrude","SWEPT_FACE",FACE,{"disambiguationData":[OSD([sQuery(id+"F4.wireOp",EDGE,"E43")])]}),makeQuery(id+"F8.opExtrude","CAP_FACE",FACE,{"disambiguationData":[OSD([sQuery(id+"F7.wireOp",EDGE,"E80")])],"isStart":false})]});
            var Q2;
            Q2=makeQuery(id+"F8.boolean.opBoolean","INTERSECT",EDGE,{"disambiguationData":[OD(1.0)],"derivedFrom":[makeQuery(id+"F5.opExtrude","SWEPT_FACE",FACE,{"disambiguationData":[OSD([sQuery(id+"F4.wireOp",EDGE,"E43")])]}),makeQuery(id+"F8.opExtrude","SWEPT_FACE",FACE,{"disambiguationData":[OSD([sQuery(id+"F7.wireOp",EDGE,"E80")])]})]});
            var Q3;
            {var subQ0=sQuery(id+"F4.wireOp",EDGE,"E43");Q3=makeQuery(id+"F8.boolean.opBoolean","SPLIT",EDGE,{"disambiguationData":[TD([makeQuery(id+"F5.opExtrude","SWEPT_FACE",FACE,{"disambiguationData":[OSD([sQuery(id+"F4.wireOp",EDGE,"E48.filletArc")])]})])],"derivedFrom":makeQuery(id+"F5.opExtrude","CAP_EDGE",EDGE,{"disambiguationData":[OSD([subQ0])],"isStart":false})});}
            var Q4;
            {var subQ0=sQuery(id+"F0.wireOp",EDGE,"E25.7");var subQ1=sQuery(id+"F0.wireOp",EDGE,"E25.1");var subQ2=sQuery(id+"F0.wireOp",EDGE,"E25.6");var subQ3=sQuery(id+"F0.wireOp",EDGE,"E25.5");var subQ4=sQuery(id+"F0.wireOp",EDGE,"E25.4");var subQ5=sQuery(id+"F0.wireOp",EDGE,"E25.0");var subQ6=sQuery(id+"F0.wireOp",EDGE,"E25.2");var subQ7=sQuery(id+"F0.wireOp",EDGE,"E25.3");Q4=makeQuery(id+"F8.boolean.opBoolean","INTERSECT",EDGE,{"derivedFrom":[makeQuery(id+"F5.boolean.opBoolean","SPLIT",FACE,{"disambiguationData":[TD([makeQuery(id+"F2.opExtrude","SWEPT_FACE",FACE,{"disambiguationData":[OSD([subQ5])]})])],"derivedFrom":makeQuery(id+"F3.boolean.opBoolean","COPY",FACE,{"derivedFrom":makeQuery(id+"F3.opExtrude","CAP_FACE",FACE,{"disambiguationData":[OSD([subQ5,subQ1,subQ6,subQ7,subQ4,subQ3,subQ2,subQ0])],"isStart":false})})}),makeQuery(id+"F8.opExtrude","SWEPT_FACE",FACE,{"disambiguationData":[OSD([sQuery(id+"F7.wireOp",EDGE,"E80")])]})]});}
            var Q5;
            Q5=makeQuery(id+"F8.boolean.opBoolean","INTERSECT",EDGE,{"disambiguationData":[OD(0.0)],"derivedFrom":[makeQuery(id+"F5.opExtrude","SWEPT_FACE",FACE,{"disambiguationData":[OSD([sQuery(id+"F4.wireOp",EDGE,"E43")])]}),makeQuery(id+"F8.opExtrude","SWEPT_FACE",FACE,{"disambiguationData":[OSD([sQuery(id+"F7.wireOp",EDGE,"E80")])]})]});
            fillet(context, id + "F14", {"entities" : qUnion([Q0, Q1, Q2, Q3, Q4, Q5]), "radius" : 3 * mm, "tangentPropagation" : true, "allowEdgeOverflow" : false});
        }
        {
            var Q0;
            Q0=makeQuery(id+"F1.opExtrude","CAP_EDGE",EDGE,{"disambiguationData":[OSD([sQuery(id+"F0.wireOp",EDGE,"E1.bottom")])],"isStart":false});
            fillet(context, id + "F15", {"entities" : qUnion([Q0]), "radius" : 2 * mm, "tangentPropagation" : true, "allowEdgeOverflow" : false});
        }
        {
            var Q0;
            Q0 = qSketchRegion(id + "F0", true);
            extrude(context, id + "F16", {"entities" : qUnion([Q0]), "operationType" : NewBodyOperationType.ADD, "depth" : 25 * mm});
        }
    });
